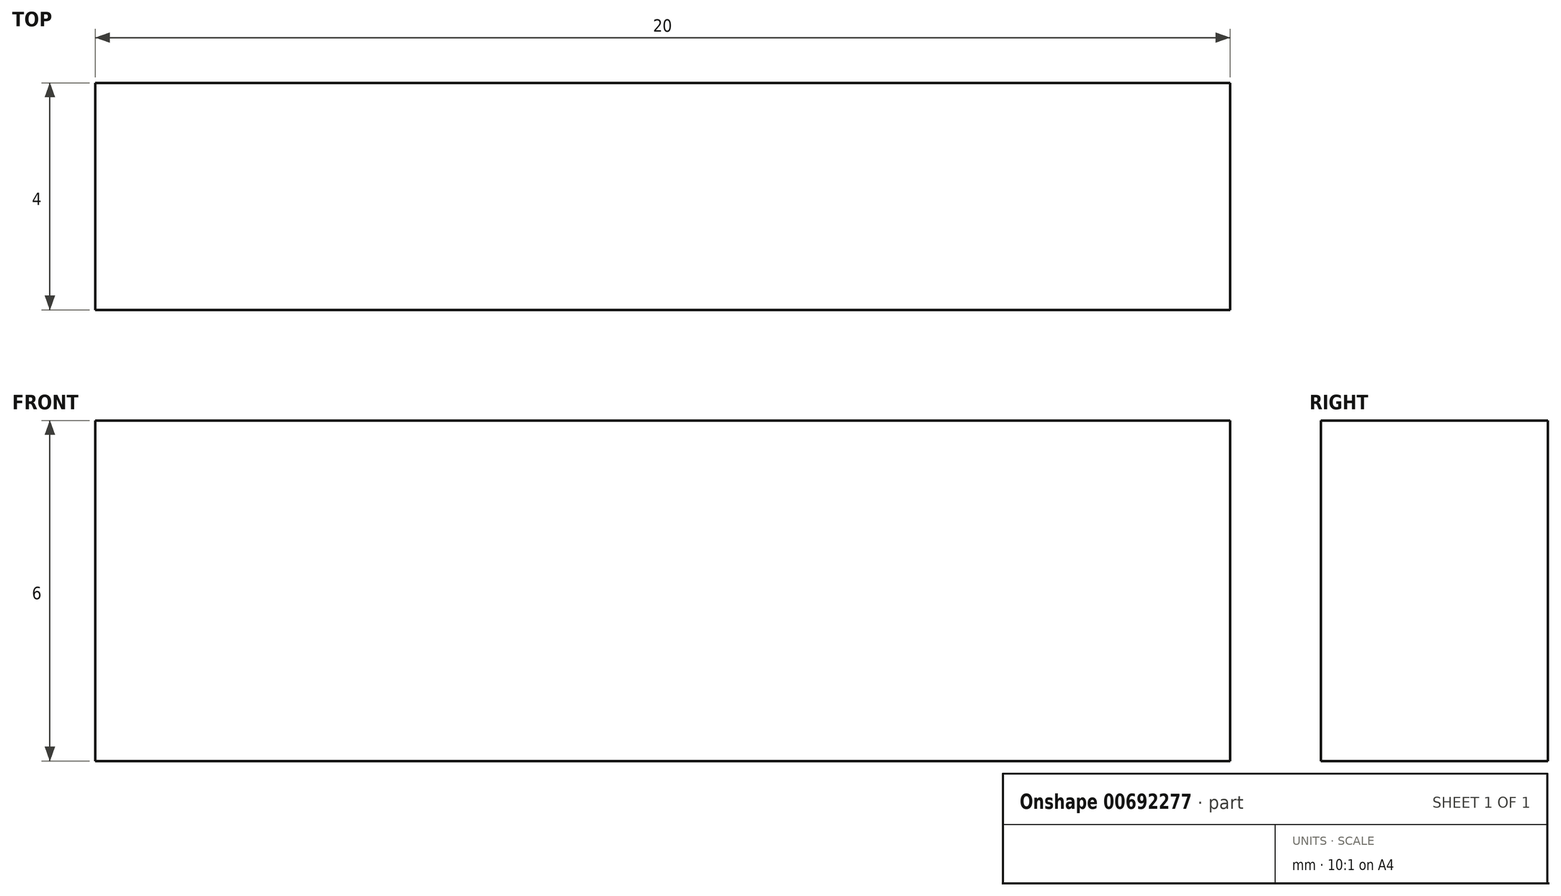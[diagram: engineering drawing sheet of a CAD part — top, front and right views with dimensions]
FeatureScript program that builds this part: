
annotation { "Feature Type Name" : "Feature", "Feature Type Description" : "" }
export const myFeature = defineFeature(function(context is Context, id is Id, definition is map)
    precondition{}
    {
        {
            var Q0;
            Q0=qCreatedBy(makeId("Top.planeOp"),FACE);
            var sketch = newSketch(context, id + "F0", { "sketchPlane" : qUnion([Q0])});
            skLineSegment(sketch, "E0.bottom", {"start": v(0, 0) * mm, "end": v(20, 0) * mm});
            skLineSegment(sketch, "E0.top", {"start": v(0, 4) * mm, "end": v(20, 4) * mm});
            skLineSegment(sketch, "E0.left", {"start": v(0, 0) * mm, "end": v(0, 4) * mm});
            skLineSegment(sketch, "E0.right", {"start": v(20, 0) * mm, "end": v(20, 4) * mm});
            skSolve(sketch);
        }
        {
            var Q0;
            Q0 = qSketchRegion(id + "F0", true);
            extrude(context, id + "F1", {"entities" : qUnion([Q0]), "depth" : 6 * mm, "offsetDistance" : 25.4 * mm});
        }
    });
